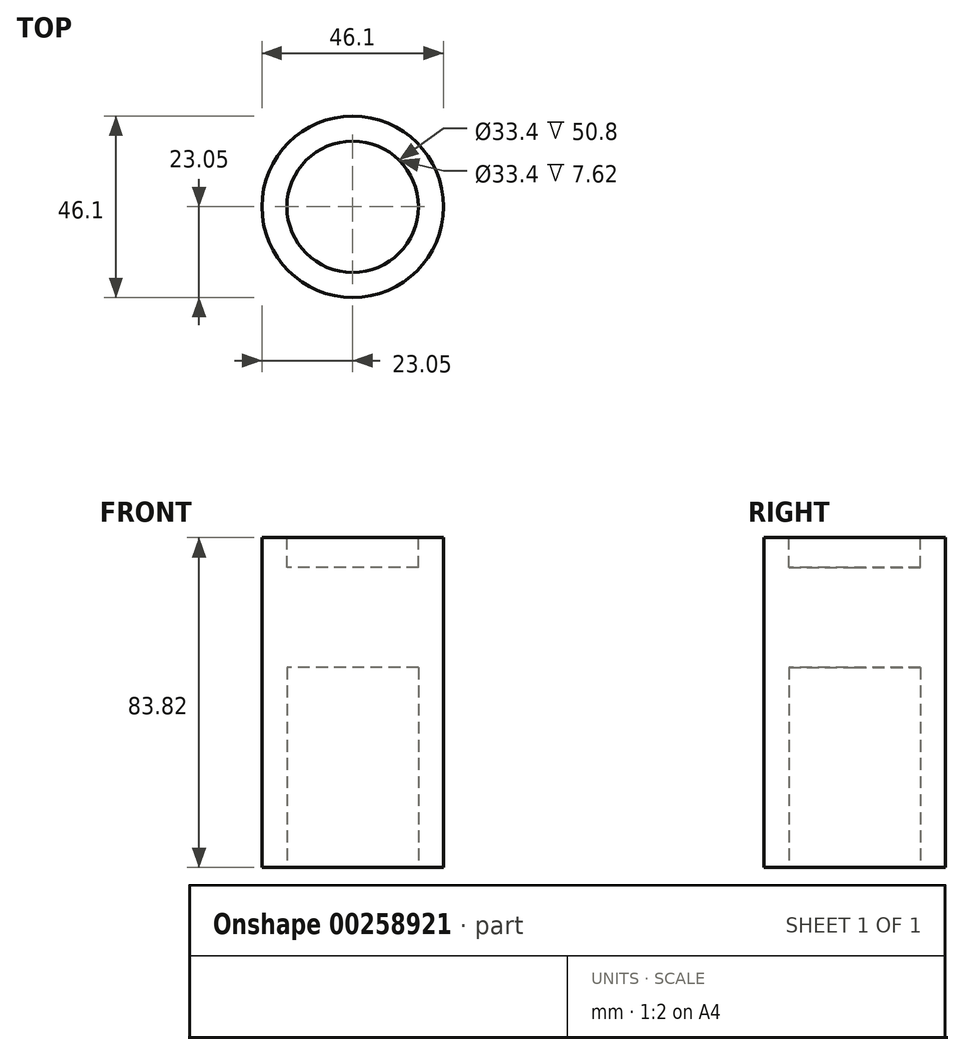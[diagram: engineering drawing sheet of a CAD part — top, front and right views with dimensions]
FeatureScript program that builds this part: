
annotation { "Feature Type Name" : "Feature", "Feature Type Description" : "" }
export const myFeature = defineFeature(function(context is Context, id is Id, definition is map)
    precondition{}
    {
        {
            var Q0;
            Q0=qCreatedBy(makeId("Top.planeOp"),FACE);
            var sketch = newSketch(context, id + "F0", { "sketchPlane" : qUnion([Q0])});
            skCircle(sketch, "E0", {"center": v(0, 0) * mm, "radius": 16.7 * mm});
            skCircle(sketch, "E1", {"center": v(0, 0) * mm, "radius": 23.05 * mm});
            skSolve(sketch);
        }
        {
            var Q0;
            Q0=makeQuery(id+"F0.imprint","IMPRINT",FACE,{"disambiguationData":[TD([[makeQuery(id+"F0.imprint","IMPRINT",EDGE,{"derivedFrom":sQuery(id+"F0.wireOp",EDGE,"E0")}),-1.0]])]});
            extrude(context, id + "F1", {"entities" : qUnion([Q0]), "depth" : 50.8 * mm});
        }
        {
            var Q0;
            Q0=makeQuery(id+"F1.opExtrude","CAP_FACE",FACE,{"disambiguationData":[OSD([sQuery(id+"F0.wireOp",EDGE,"E0"),sQuery(id+"F0.wireOp",EDGE,"E1")])],"isStart":false});
            var sketch = newSketch(context, id + "F2", { "sketchPlane" : qUnion([Q0])});
            skCircle(sketch, "E2", {"center": v(0, 0) * mm, "radius": 23.05 * mm});
            skSolve(sketch);
        }
        {
            var Q0;
            Q0 = qSketchRegion(id + "F2", true);
            extrude(context, id + "F3", {"entities" : qUnion([Q0]), "operationType" : NewBodyOperationType.ADD, "depth" : 25.4 * mm});
        }
        {
            var Q0;
            Q0=makeQuery(id+"F3.opExtrude","CAP_FACE",FACE,{"disambiguationData":[OSD([sQuery(id+"F2.wireOp",EDGE,"E2")])],"isStart":false});
            extrude(context, id + "F4", {"entities" : qUnion([Q0]), "operationType" : NewBodyOperationType.ADD, "depth" : 7.62 * mm});
        }
        {
            var Q0;
            Q0=makeQuery(id+"F4.opExtrude","CAP_FACE",FACE,{"disambiguationData":[OSD([sQuery(id+"F2.wireOp",EDGE,"E2")])],"isStart":false});
            var sketch = newSketch(context, id + "F5", { "sketchPlane" : qUnion([Q0])});
            skCircle(sketch, "E3", {"center": v(0, 0) * mm, "radius": 16.7 * mm});
            skSolve(sketch);
        }
        {
            var Q0;
            Q0 = qSketchRegion(id + "F5", true);
            extrude(context, id + "F6", {"entities" : qUnion([Q0]), "operationType" : NewBodyOperationType.REMOVE, "oppositeDirection" : true, "depth" : 7.62 * mm});
        }
    });
